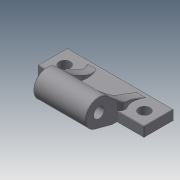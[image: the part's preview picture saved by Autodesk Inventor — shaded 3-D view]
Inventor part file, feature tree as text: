
AUTODESK INVENTOR PART (.ipt)
format: ipt  version: 2020.3 (Build 243373000, 373)  size: 302,080 bytes
history: native  units: in
note: dims shown in document units (in); Inventor stores cm internally (conversion verified against a paired STEP export)
features: fillet x2, revolve x1
ambient origin geometry x8: Origin, YZ Plane, XZ Plane, XY Plane, X Axis, Y Axis, Z Axis, Center Point
bodies: Solid1 (feature_tree), Solid2 (feature_tree), Solid3 (feature_tree)
feature tree (3):
  fillet  "Fillet5"  [1 undecoded]
  fillet  "Fillet4"  [1 undecoded]
  revolve  "Revolve1"  [1 undecoded]
note: 3 required parameter values undecoded (feature->parameter linkage not recoverable at this tier; creation-order binding heuristic only, values carry confidence <= 0.55)
